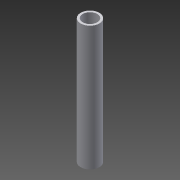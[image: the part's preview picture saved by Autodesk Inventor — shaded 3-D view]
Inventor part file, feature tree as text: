
AUTODESK INVENTOR PART (.ipt)
format: ipt  version: 2015 (Build 190159000, 159)  size: 84,992 bytes
history: native  units: mm
features: other x2, extrude x1, shell x1, sketch x1
ambient origin geometry x8: Origin, YZ Plane, XZ Plane, XY Plane, X Axis, Y Axis, Z Axis, Center Point
bodies: Body1 (feature_tree)
feature tree (5):
  other  "Bryła1"
  other  "Płaszczyzna konstrukcyjna1"
  extrude  "Wyciągnięcie proste1"  [1 undecoded]
  shell  "Skorupa2"  Thickness=18.0mm
  sketch  "Szkic1"
note: 1 required parameter value undecoded (feature->parameter linkage not recoverable at this tier; creation-order binding heuristic only, values carry confidence <= 0.55)
